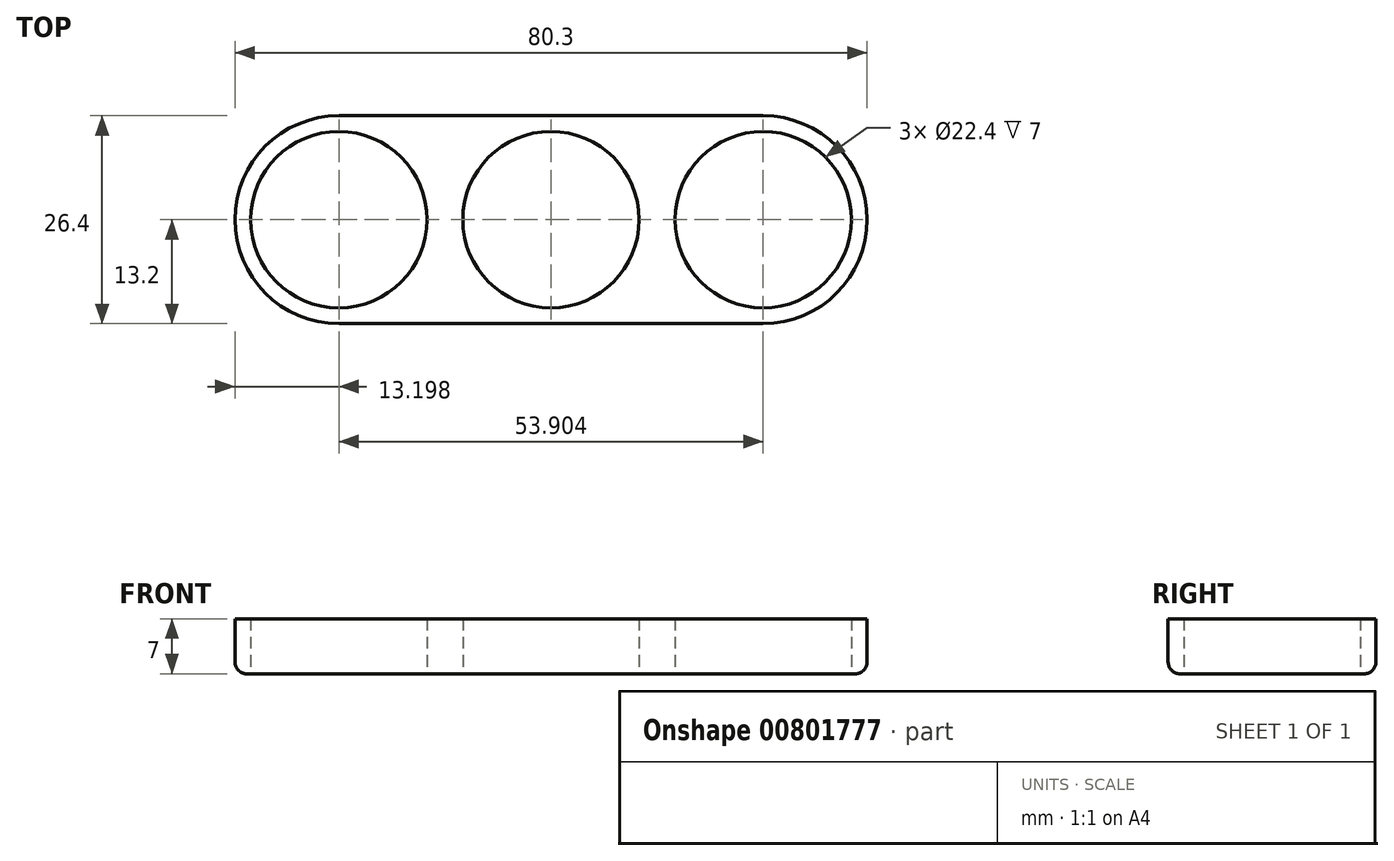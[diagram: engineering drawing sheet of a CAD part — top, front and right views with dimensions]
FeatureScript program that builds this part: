
annotation { "Feature Type Name" : "Feature", "Feature Type Description" : "" }
export const myFeature = defineFeature(function(context is Context, id is Id, definition is map)
    precondition{}
    {
        {
            var Q0;
            Q0=qCreatedBy(makeId("Top.planeOp"),FACE);
            var sketch = newSketch(context, id + "F0", { "sketchPlane" : qUnion([Q0])});
            skCircle(sketch, "E0", {"center": v(0, 0) * mm, "radius": 11.2 * mm});
            skCircle(sketch, "E1", {"center": v(-26.95, 0) * mm, "radius": 11.2 * mm});
            skCircle(sketch, "E2.1.0", {"center": v(26.95, 0) * mm, "radius": 11.2 * mm});
            skArc(sketch, "E3", {"start": v(-26.95, 13.2) * mm, "mid": v(-40.15, 0) * mm, "end": v(-26.95, -13.2) * mm});
            skArc(sketch, "E4.1.0", {"start": v(26.95, -13.2) * mm, "mid": v(40.15, 0) * mm, "end": v(26.95, 13.2) * mm});
            skLineSegment(sketch, "E5", {"start": v(0, 13.2) * mm, "end": v(-26.95, 13.2) * mm});
            skLineSegment(sketch, "E6", {"start": v(0, 13.2) * mm, "end": v(26.95, 13.2) * mm});
            skLineSegment(sketch, "E7", {"start": v(0, -13.2) * mm, "end": v(-26.95, -13.2) * mm});
            skLineSegment(sketch, "E8", {"start": v(0, -13.2) * mm, "end": v(26.95, -13.2) * mm});
            skSolve(sketch);
        }
        {
            var Q0;
            Q0=makeQuery(id+"F0.imprint","IMPRINT",FACE,{"disambiguationData":[TD([[makeQuery(id+"F0.imprint","IMPRINT",EDGE,{"derivedFrom":sQuery(id+"F0.wireOp",EDGE,"E0")}),-1.0]])]});
            extrude(context, id + "F1", {"entities" : qUnion([Q0]), "depth" : 7 * mm, "offsetDistance" : 25 * mm});
        }
        {
            var Q0;
            Q0=makeQuery(id+"F1.opExtrude","CAP_EDGE",EDGE,{"disambiguationData":[OSD([sQuery(id+"F0.wireOp",EDGE,"E5"),sQuery(id+"F0.wireOp",EDGE,"E6")])],"isStart":true});
            var Q1;
            Q1=makeQuery(id+"F1.opExtrude","CAP_EDGE",EDGE,{"disambiguationData":[OSD([sQuery(id+"F0.wireOp",EDGE,"E3")])],"isStart":true});
            var Q2;
            Q2=makeQuery(id+"F1.opExtrude","CAP_EDGE",EDGE,{"disambiguationData":[OSD([sQuery(id+"F0.wireOp",EDGE,"E7"),sQuery(id+"F0.wireOp",EDGE,"E8")])],"isStart":true});
            var Q3;
            Q3=makeQuery(id+"F1.opExtrude","CAP_EDGE",EDGE,{"disambiguationData":[OSD([sQuery(id+"F0.wireOp",EDGE,"E4.1.0")])],"isStart":true});
            fillet(context, id + "F2", {"entities" : qUnion([Q0, Q1, Q2, Q3]), "radius" : 1.5 * mm, "tangentPropagation" : true, "allowEdgeOverflow" : false});
        }
    });
